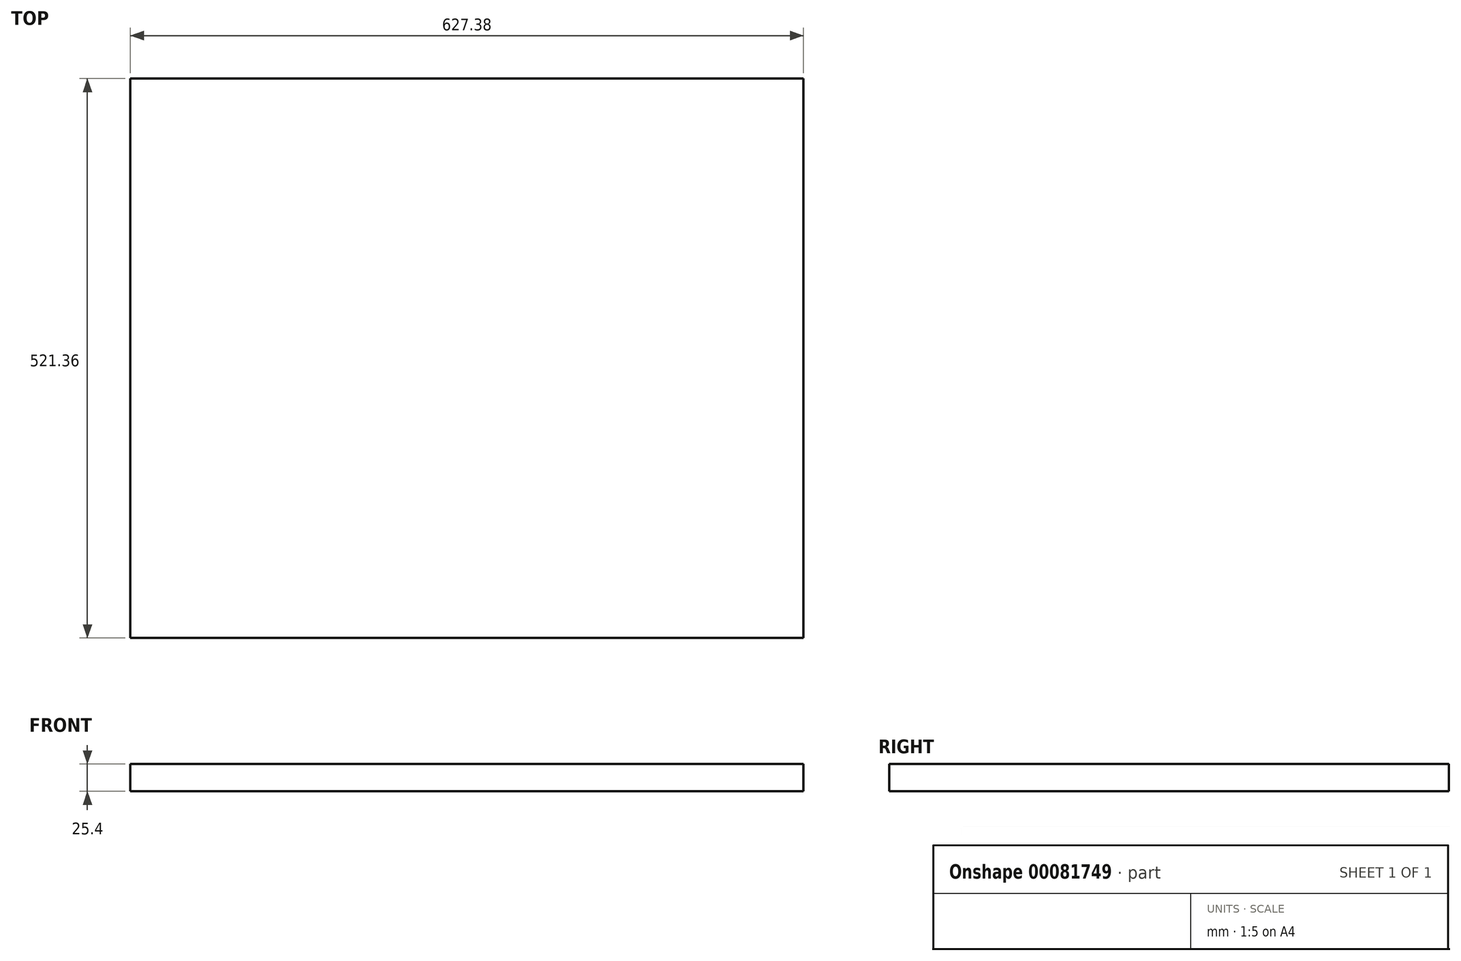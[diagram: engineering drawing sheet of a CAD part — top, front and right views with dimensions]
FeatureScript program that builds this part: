
annotation { "Feature Type Name" : "Feature", "Feature Type Description" : "" }
export const myFeature = defineFeature(function(context is Context, id is Id, definition is map)
    precondition{}
    {
        {
            var Q0;
            Q0=qCreatedBy(makeId("Top.planeOp"),FACE);
            var sketch = newSketch(context, id + "F0", { "sketchPlane" : qUnion([Q0])});
            skLineSegment(sketch, "E0.bottom", {"start": v(-316.2, 372.28) * mm, "end": v(311.17, 372.28) * mm});
            skLineSegment(sketch, "E0.top", {"start": v(-316.2, -149.08) * mm, "end": v(311.17, -149.08) * mm});
            skLineSegment(sketch, "E0.left", {"start": v(-316.2, 372.28) * mm, "end": v(-316.2, -149.08) * mm});
            skLineSegment(sketch, "E0.right", {"start": v(311.17, 372.28) * mm, "end": v(311.17, -149.08) * mm});
            skSolve(sketch);
        }
        {
            var Q0;
            Q0 = qSketchRegion(id + "F0", true);
            extrude(context, id + "F1", {"entities" : qUnion([Q0]), "depth" : 25.4 * mm, "offsetDistance" : 25.4 * mm});
        }
    });
